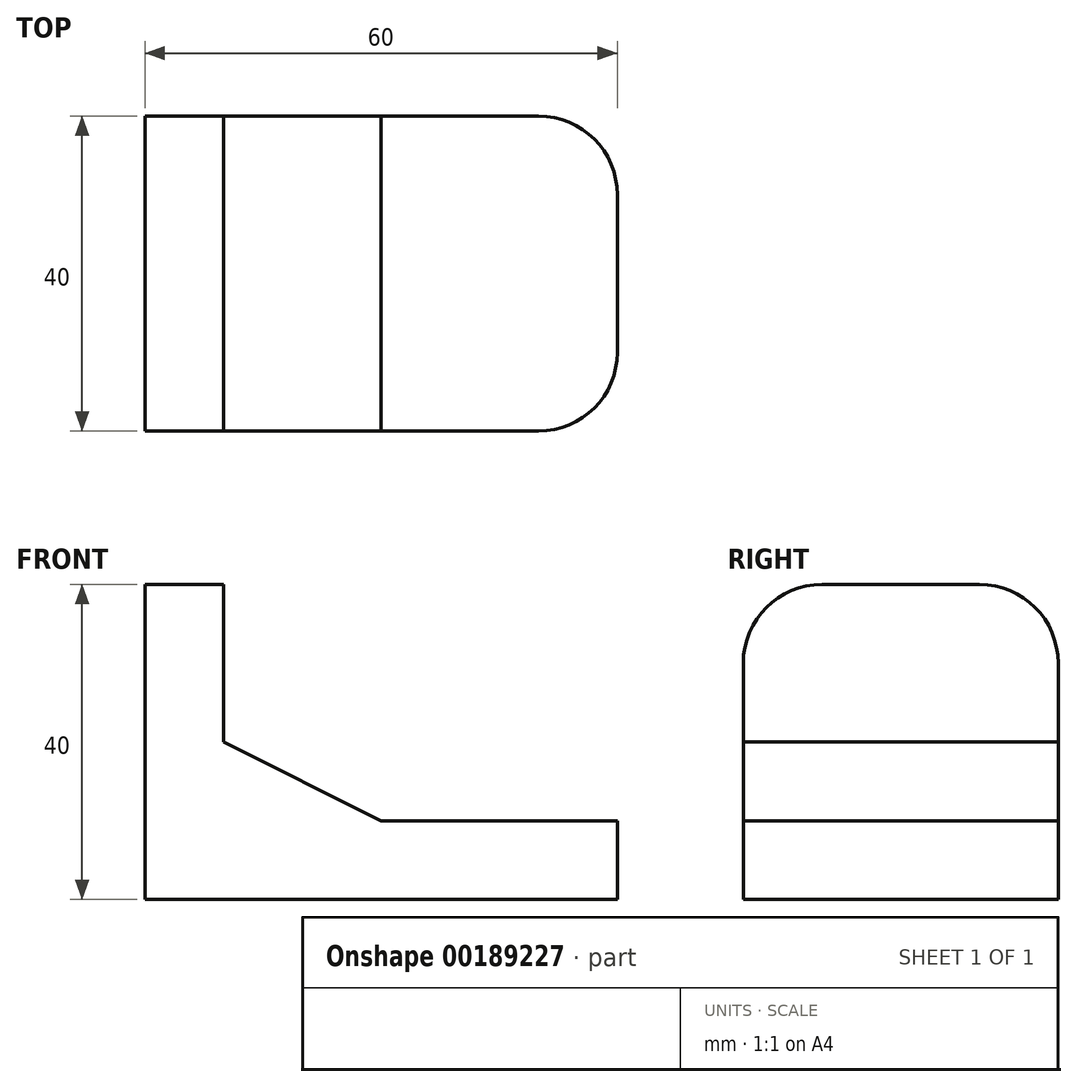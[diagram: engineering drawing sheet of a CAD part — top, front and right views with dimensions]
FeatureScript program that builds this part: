
annotation { "Feature Type Name" : "Feature", "Feature Type Description" : "" }
export const myFeature = defineFeature(function(context is Context, id is Id, definition is map)
    precondition{}
    {
        {
            var Q0;
            Q0=qCreatedBy(makeId("Front.planeOp"),FACE);
            var sketch = newSketch(context, id + "F0", { "sketchPlane" : qUnion([Q0])});
            skLineSegment(sketch, "E0", {"start": v(0, 0) * mm, "end": v(60, 0) * mm});
            skLineSegment(sketch, "E1", {"start": v(60, 0) * mm, "end": v(60, 10) * mm});
            skLineSegment(sketch, "E2", {"start": v(60, 10) * mm, "end": v(30, 10) * mm});
            skLineSegment(sketch, "E3", {"start": v(30, 10) * mm, "end": v(10, 20) * mm});
            skLineSegment(sketch, "E4", {"start": v(10, 20) * mm, "end": v(10, 40) * mm});
            skLineSegment(sketch, "E5", {"start": v(10, 40) * mm, "end": v(0, 40) * mm});
            skLineSegment(sketch, "E6", {"start": v(0, 40) * mm, "end": v(0, 0) * mm});
            skSolve(sketch);
        }
        {
            var Q0;
            Q0=makeQuery(id+"F0.imprint","IMPRINT",FACE,{"disambiguationData":[TD([[makeQuery(id+"F0.imprint","IMPRINT",EDGE,{"derivedFrom":sQuery(id+"F0.wireOp",EDGE,"E0")}),1.0]])]});
            extrude(context, id + "F1", {"entities" : qUnion([Q0]), "endBound" : BoundingType.SYMMETRIC, "depth" : 40 * mm});
        }
        {
            var Q0;
            Q0=makeQuery(id+"F1.opExtrude","CAP_EDGE",EDGE,{"disambiguationData":[OSD([sQuery(id+"F0.wireOp",EDGE,"E5")])],"isStart":false});
            var Q1;
            Q1=makeQuery(id+"F1.opExtrude","CAP_EDGE",EDGE,{"disambiguationData":[OSD([sQuery(id+"F0.wireOp",EDGE,"E5")])],"isStart":true});
            var Q2;
            Q2=makeQuery(id+"F1.opExtrude","CAP_EDGE",EDGE,{"disambiguationData":[OSD([sQuery(id+"F0.wireOp",EDGE,"E1")])],"isStart":false});
            var Q3;
            Q3=makeQuery(id+"F1.opExtrude","CAP_EDGE",EDGE,{"disambiguationData":[OSD([sQuery(id+"F0.wireOp",EDGE,"E1")])],"isStart":true});
            fillet(context, id + "F2", {"entities" : qUnion([Q0, Q1, Q2, Q3]), "radius" : 10 * mm, "tangentPropagation" : true, "allowEdgeOverflow" : false});
        }
    });
